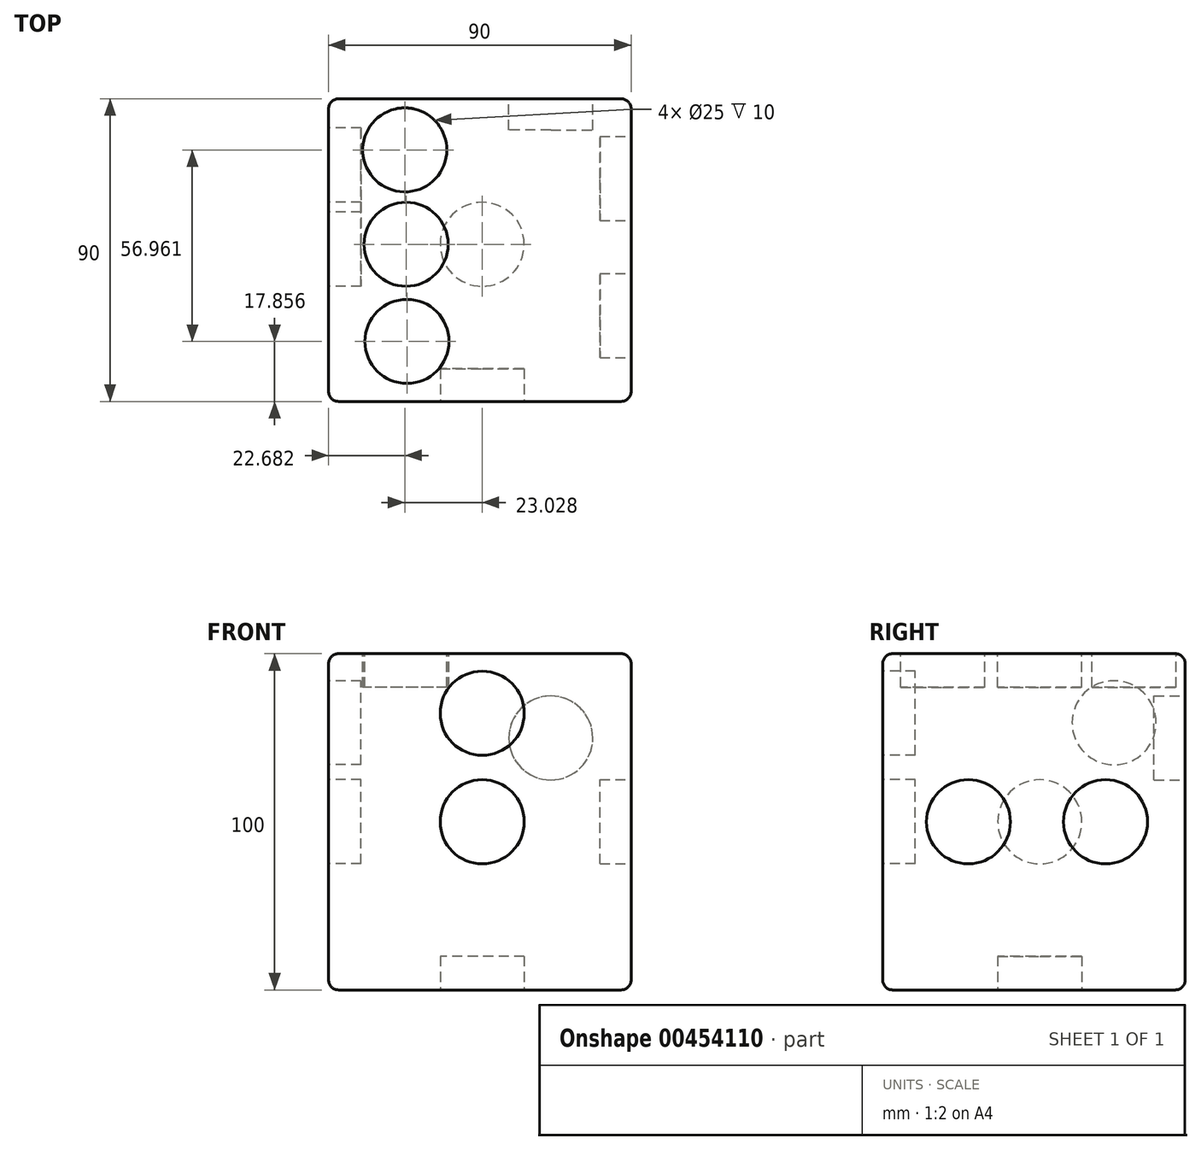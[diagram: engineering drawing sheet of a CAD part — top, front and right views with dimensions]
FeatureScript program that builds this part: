
annotation { "Feature Type Name" : "Feature", "Feature Type Description" : "" }
export const myFeature = defineFeature(function(context is Context, id is Id, definition is map)
    precondition{}
    {
        {
            var Q0;
            Q0=qCreatedBy(makeId("Top.planeOp"),FACE);
            var sketch = newSketch(context, id + "F0", { "sketchPlane" : qUnion([Q0])});
            skLineSegment(sketch, "E0.bottom", {"start": v(-45.7, 43.25) * mm, "end": v(44.3, 43.25) * mm});
            skLineSegment(sketch, "E0.top", {"start": v(-45.7, -46.75) * mm, "end": v(44.3, -46.75) * mm});
            skLineSegment(sketch, "E0.left", {"start": v(-45.7, 43.25) * mm, "end": v(-45.7, -46.75) * mm});
            skLineSegment(sketch, "E0.right", {"start": v(44.3, 43.25) * mm, "end": v(44.3, -46.75) * mm});
            skSolve(sketch);
        }
        {
            var Q0;
            Q0=makeQuery(id+"F0.imprint","IMPRINT",FACE,{"disambiguationData":[TD([[makeQuery(id+"F0.imprint","IMPRINT",EDGE,{"derivedFrom":sQuery(id+"F0.wireOp",EDGE,"E0.bottom")}),-1.0]])]});
            extrude(context, id + "F1", {"entities" : qUnion([Q0]), "depth" : 50 * mm, "offsetDistance" : 25 * mm});
        }
        {
            var Q0;
            Q0=makeQuery(id+"F1.opExtrude","SWEPT_BODY",BODY,{"disambiguationData":[OSD([sQuery(id+"F0.wireOp",EDGE,"E0.bottom"),sQuery(id+"F0.wireOp",EDGE,"E0.top"),sQuery(id+"F0.wireOp",EDGE,"E0.left"),sQuery(id+"F0.wireOp",EDGE,"E0.right")])]});
            var Q1;
            Q1=qCreatedBy(makeId("Top.planeOp"),FACE);
            mirror(context, id + "F2", {"operationType" : NewBodyOperationType.ADD, "entities" : qUnion([Q0]), "mirrorPlane" : qUnion([Q1])});
        }
        {
            var Q0;
            Q0=qCreatedBy(makeId("Top.planeOp"),FACE);
            cPlane(context, id + "F3", {"entities" : qUnion([Q0]), "cplaneType" : CPlaneType.OFFSET, "offset" : 50 * mm, "width" : 150 * mm, "height" : 150 * mm});
        }
        {
            var Q0;
            Q0=qCreatedBy(makeId("Top.planeOp"),FACE);
            cPlane(context, id + "F4", {"entities" : qUnion([Q0]), "cplaneType" : CPlaneType.OFFSET, "offset" : 50 * mm, "oppositeDirection" : true, "width" : 150 * mm, "height" : 150 * mm});
        }
        {
            var Q0;
            Q0=qCreatedBy(id+"F4.planeOp",FACE);
            var sketch = newSketch(context, id + "F5", { "sketchPlane" : qUnion([Q0])});
            skCircle(sketch, "E1", {"center": v(0, 0) * mm, "radius": 12.5 * mm});
            skSolve(sketch);
        }
        {
            var Q0;
            Q0 = qSketchRegion(id + "F5", true);
            extrude(context, id + "F6", {"entities" : qUnion([Q0]), "operationType" : NewBodyOperationType.REMOVE, "depth" : 10 * mm});
        }
        {
            var Q0;
            Q0=qCreatedBy(id+"F3.planeOp",FACE);
            var sketch = newSketch(context, id + "F7", { "sketchPlane" : qUnion([Q0])});
            skCircle(sketch, "E2", {"center": v(-22.63, 0) * mm, "radius": 12.5 * mm});
            skSolve(sketch);
        }
        {
            var Q0;
            Q0 = qSketchRegion(id + "F7", true);
            extrude(context, id + "F8", {"entities" : qUnion([Q0]), "operationType" : NewBodyOperationType.REMOVE, "oppositeDirection" : true, "depth" : 10 * mm});
        }
        {
            var Q0;
            Q0=qCreatedBy(id+"F3.planeOp",FACE);
            var sketch = newSketch(context, id + "F9", { "sketchPlane" : qUnion([Q0])});
            skCircle(sketch, "E3", {"center": v(-23.03, 28.07) * mm, "radius": 12.5 * mm});
            skSolve(sketch);
        }
        {
            var Q0;
            Q0 = qSketchRegion(id + "F9", true);
            extrude(context, id + "F10", {"entities" : qUnion([Q0]), "operationType" : NewBodyOperationType.REMOVE, "oppositeDirection" : true, "depth" : 10 * mm});
        }
        {
            var Q0;
            Q0=qCreatedBy(id+"F3.planeOp",FACE);
            var sketch = newSketch(context, id + "F11", { "sketchPlane" : qUnion([Q0])});
            skCircle(sketch, "E4", {"center": v(-22.38, -28.9) * mm, "radius": 12.5 * mm});
            skSolve(sketch);
        }
        {
            var Q0;
            Q0 = qSketchRegion(id + "F11", true);
            extrude(context, id + "F12", {"entities" : qUnion([Q0]), "operationType" : NewBodyOperationType.REMOVE, "oppositeDirection" : true, "depth" : 10 * mm});
        }
        {
            var Q0;
            Q0=qCreatedBy(makeId("Right.planeOp"),FACE);
            cPlane(context, id + "F13", {"entities" : qUnion([Q0]), "cplaneType" : CPlaneType.OFFSET, "offset" : 45 * mm, "width" : 150 * mm, "height" : 150 * mm});
        }
        {
            var Q0;
            Q0=qCreatedBy(makeId("Right.planeOp"),FACE);
            cPlane(context, id + "F14", {"entities" : qUnion([Q0]), "cplaneType" : CPlaneType.OFFSET, "offset" : 46 * mm, "oppositeDirection" : true, "width" : 150 * mm, "height" : 150 * mm});
        }
        {
            var Q0;
            Q0=qCreatedBy(id+"F13.planeOp",FACE);
            var sketch = newSketch(context, id + "F15", { "sketchPlane" : qUnion([Q0])});
            skCircle(sketch, "E5", {"center": v(-21.25, 0) * mm, "radius": 12.5 * mm});
            skSolve(sketch);
        }
        {
            var Q0;
            Q0 = qSketchRegion(id + "F15", true);
            extrude(context, id + "F16", {"entities" : qUnion([Q0]), "operationType" : NewBodyOperationType.REMOVE, "oppositeDirection" : true, "depth" : 10 * mm});
        }
        {
            var Q0;
            Q0=qCreatedBy(id+"F13.planeOp",FACE);
            var sketch = newSketch(context, id + "F17", { "sketchPlane" : qUnion([Q0])});
            skCircle(sketch, "E6", {"center": v(19.54, 0) * mm, "radius": 12.5 * mm});
            skSolve(sketch);
        }
        {
            var Q0;
            Q0 = qSketchRegion(id + "F17", true);
            extrude(context, id + "F18", {"entities" : qUnion([Q0]), "operationType" : NewBodyOperationType.REMOVE, "oppositeDirection" : true, "depth" : 10 * mm});
        }
        {
            var Q0;
            Q0=qCreatedBy(id+"F14.planeOp",FACE);
            var sketch = newSketch(context, id + "F19", { "sketchPlane" : qUnion([Q0])});
            skCircle(sketch, "E7", {"center": v(0, 0) * mm, "radius": 12.5 * mm});
            skSolve(sketch);
        }
        {
            var Q0;
            Q0 = qSketchRegion(id + "F19", true);
            extrude(context, id + "F20", {"entities" : qUnion([Q0]), "operationType" : NewBodyOperationType.REMOVE, "depth" : 10 * mm});
        }
        {
            var Q0;
            Q0=qCreatedBy(id+"F14.planeOp",FACE);
            var sketch = newSketch(context, id + "F21", { "sketchPlane" : qUnion([Q0])});
            skCircle(sketch, "E8", {"center": v(22.1, 29.46) * mm, "radius": 12.5 * mm});
            skSolve(sketch);
        }
        {
            var Q0;
            Q0 = qSketchRegion(id + "F21", true);
            extrude(context, id + "F22", {"entities" : qUnion([Q0]), "operationType" : NewBodyOperationType.REMOVE, "depth" : 10 * mm});
        }
        {
            var Q0;
            Q0=qCreatedBy(makeId("Front.planeOp"),FACE);
            cPlane(context, id + "F23", {"entities" : qUnion([Q0]), "cplaneType" : CPlaneType.OFFSET, "offset" : 47 * mm, "width" : 150 * mm, "height" : 150 * mm});
        }
        {
            var Q0;
            Q0=qCreatedBy(makeId("Front.planeOp"),FACE);
            cPlane(context, id + "F24", {"entities" : qUnion([Q0]), "cplaneType" : CPlaneType.OFFSET, "offset" : 44 * mm, "oppositeDirection" : true, "width" : 150 * mm, "height" : 150 * mm});
        }
        {
            var Q0;
            Q0=qCreatedBy(id+"F23.planeOp",FACE);
            var sketch = newSketch(context, id + "F25", { "sketchPlane" : qUnion([Q0])});
            skCircle(sketch, "E9", {"center": v(0, 0) * mm, "radius": 12.5 * mm});
            skSolve(sketch);
        }
        {
            var Q0;
            Q0 = qSketchRegion(id + "F25", true);
            extrude(context, id + "F26", {"entities" : qUnion([Q0]), "operationType" : NewBodyOperationType.REMOVE, "oppositeDirection" : true, "depth" : 10 * mm});
        }
        {
            var Q0;
            Q0=qCreatedBy(id+"F23.planeOp",FACE);
            var sketch = newSketch(context, id + "F27", { "sketchPlane" : qUnion([Q0])});
            skCircle(sketch, "E10", {"center": v(0, 32.3) * mm, "radius": 12.5 * mm});
            skSolve(sketch);
        }
        {
            var Q0;
            Q0 = qSketchRegion(id + "F27", true);
            extrude(context, id + "F28", {"entities" : qUnion([Q0]), "operationType" : NewBodyOperationType.REMOVE, "oppositeDirection" : true, "depth" : 10 * mm});
        }
        {
            var Q0;
            Q0=qCreatedBy(id+"F24.planeOp",FACE);
            var sketch = newSketch(context, id + "F29", { "sketchPlane" : qUnion([Q0])});
            skCircle(sketch, "E11", {"center": v(20.4, 24.93) * mm, "radius": 12.5 * mm});
            skSolve(sketch);
        }
        {
            var Q0;
            Q0 = qSketchRegion(id + "F29", true);
            extrude(context, id + "F30", {"entities" : qUnion([Q0]), "operationType" : NewBodyOperationType.REMOVE, "depth" : 10 * mm});
        }
        {
            var Q0;
            Q0=makeQuery(id+"F1.opExtrude","CAP_EDGE",EDGE,{"disambiguationData":[OSD([sQuery(id+"F0.wireOp",EDGE,"E0.right")])],"isStart":false});
            var Q1;
            {var subQ0=makeQuery(id+"F1.opExtrude","SWEPT_EDGE",EDGE,{"disambiguationData":[OSD([sQuery(id+"F0.wireOp",EDGE,"E0.top"),sQuery(id+"F0.wireOp",EDGE,"E0.right")])]});Q1=makeQuery(id+"F2.boolean.opBoolean","MERGE",EDGE,{"derivedFrom":[subQ0,makeQuery(id+"F2.opPattern","COPY",EDGE,{"derivedFrom":subQ0,"instanceName":"1"})]});}
            var Q2;
            Q2=makeQuery(id+"F2.opPattern","COPY",EDGE,{"derivedFrom":makeQuery(id+"F1.opExtrude","CAP_EDGE",EDGE,{"disambiguationData":[OSD([sQuery(id+"F0.wireOp",EDGE,"E0.right")])],"isStart":false}),"instanceName":"1"});
            var Q3;
            {var subQ0=makeQuery(id+"F1.opExtrude","SWEPT_EDGE",EDGE,{"disambiguationData":[OSD([sQuery(id+"F0.wireOp",EDGE,"E0.bottom"),sQuery(id+"F0.wireOp",EDGE,"E0.right")])]});Q3=makeQuery(id+"F2.boolean.opBoolean","MERGE",EDGE,{"derivedFrom":[subQ0,makeQuery(id+"F2.opPattern","COPY",EDGE,{"derivedFrom":subQ0,"instanceName":"1"})]});}
            var Q4;
            Q4=makeQuery(id+"F2.opPattern","COPY",EDGE,{"derivedFrom":makeQuery(id+"F1.opExtrude","CAP_EDGE",EDGE,{"disambiguationData":[OSD([sQuery(id+"F0.wireOp",EDGE,"E0.bottom")])],"isStart":false}),"instanceName":"1"});
            var Q5;
            {var subQ0=makeQuery(id+"F1.opExtrude","SWEPT_EDGE",EDGE,{"disambiguationData":[OSD([sQuery(id+"F0.wireOp",EDGE,"E0.bottom"),sQuery(id+"F0.wireOp",EDGE,"E0.left")])]});Q5=makeQuery(id+"F2.boolean.opBoolean","MERGE",EDGE,{"derivedFrom":[subQ0,makeQuery(id+"F2.opPattern","COPY",EDGE,{"derivedFrom":subQ0,"instanceName":"1"})]});}
            var Q6;
            Q6=makeQuery(id+"F1.opExtrude","CAP_EDGE",EDGE,{"disambiguationData":[OSD([sQuery(id+"F0.wireOp",EDGE,"E0.bottom")])],"isStart":false});
            var Q7;
            Q7=makeQuery(id+"F1.opExtrude","CAP_EDGE",EDGE,{"disambiguationData":[OSD([sQuery(id+"F0.wireOp",EDGE,"E0.top")])],"isStart":false});
            var Q8;
            Q8=makeQuery(id+"F1.opExtrude","CAP_EDGE",EDGE,{"disambiguationData":[OSD([sQuery(id+"F0.wireOp",EDGE,"E0.left")])],"isStart":false});
            var Q9;
            Q9=makeQuery(id+"F2.opPattern","COPY",EDGE,{"derivedFrom":makeQuery(id+"F1.opExtrude","CAP_EDGE",EDGE,{"disambiguationData":[OSD([sQuery(id+"F0.wireOp",EDGE,"E0.top")])],"isStart":false}),"instanceName":"1"});
            var Q10;
            {var subQ0=makeQuery(id+"F1.opExtrude","SWEPT_EDGE",EDGE,{"disambiguationData":[OSD([sQuery(id+"F0.wireOp",EDGE,"E0.top"),sQuery(id+"F0.wireOp",EDGE,"E0.left")])]});Q10=makeQuery(id+"F2.boolean.opBoolean","MERGE",EDGE,{"derivedFrom":[subQ0,makeQuery(id+"F2.opPattern","COPY",EDGE,{"derivedFrom":subQ0,"instanceName":"1"})]});}
            var Q11;
            Q11=makeQuery(id+"F2.opPattern","COPY",EDGE,{"derivedFrom":makeQuery(id+"F1.opExtrude","CAP_EDGE",EDGE,{"disambiguationData":[OSD([sQuery(id+"F0.wireOp",EDGE,"E0.left")])],"isStart":false}),"instanceName":"1"});
            fillet(context, id + "F31", {"entities" : qUnion([Q0, Q1, Q2, Q3, Q4, Q5, Q6, Q7, Q8, Q9, Q10, Q11]), "radius" : 3 * mm, "tangentPropagation" : true, "allowEdgeOverflow" : false});
        }
    });
